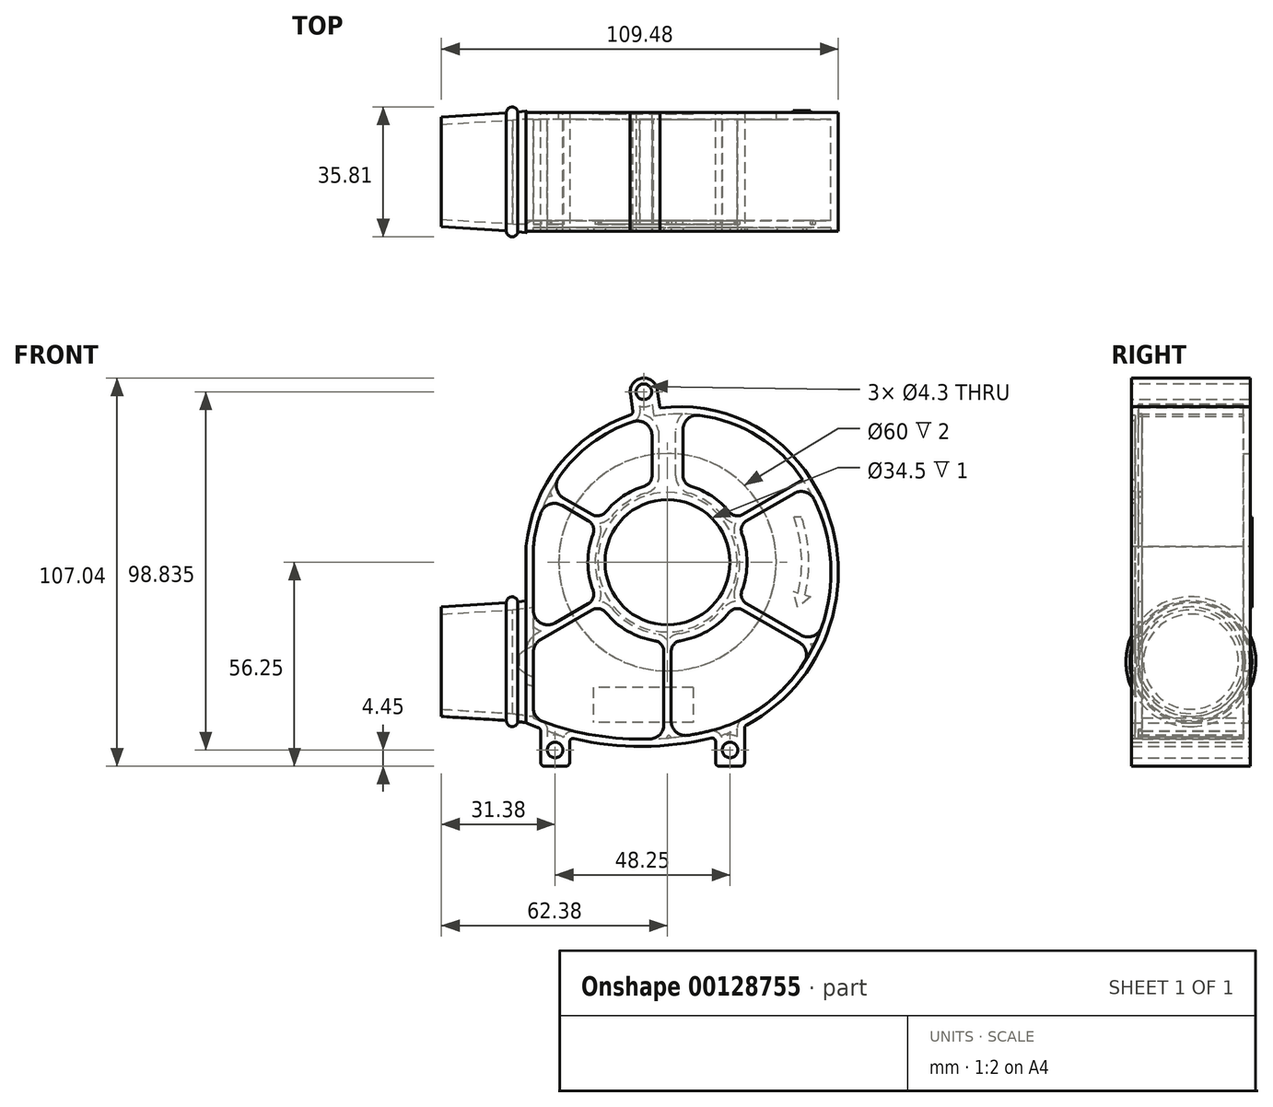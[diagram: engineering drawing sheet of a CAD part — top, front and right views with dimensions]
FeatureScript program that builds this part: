
annotation { "Feature Type Name" : "Feature", "Feature Type Description" : "" }
export const myFeature = defineFeature(function(context is Context, id is Id, definition is map)
    precondition{}
    {
        {
            var Q0;
            Q0=qCreatedBy(makeId("Front.planeOp"),FACE);
            var sketch = newSketch(context, id + "F0", { "sketchPlane" : qUnion([Q0])});
            skLineSegment(sketch, "E0", {"start": v(0, 0) * mm, "end": v(0, 15) * mm, "construction": true});
            skLineSegment(sketch, "E1", {"start": v(0, 15) * mm, "end": v(7.5, 13) * mm, "construction": true});
            skLineSegment(sketch, "E2", {"start": v(7.5, 13) * mm, "end": v(0, 0) * mm, "construction": true});
            skCircle(sketch, "E3.cCircle", {"center": v(0, 0) * mm, "radius": 220.7 * mm, "construction": true});
            skLineSegment(sketch, "E3.0", {"start": v(0, 254.83) * mm, "end": v(220.7, 127.42) * mm, "construction": true});
            skLineSegment(sketch, "E3.1", {"start": v(220.7, 127.42) * mm, "end": v(220.7, -127.42) * mm, "construction": true});
            skLineSegment(sketch, "E3.2", {"start": v(220.7, -127.42) * mm, "end": v(0, -254.83) * mm, "construction": true});
            skLineSegment(sketch, "E3.3", {"start": v(0, -254.83) * mm, "end": v(-220.7, -127.42) * mm, "construction": true});
            skLineSegment(sketch, "E3.4", {"start": v(-220.7, -127.42) * mm, "end": v(-220.7, 127.42) * mm, "construction": true});
            skLineSegment(sketch, "E3.5", {"start": v(-220.7, 127.42) * mm, "end": v(0, 254.83) * mm, "construction": true});
            skPoint(sketch, "E3.0.midPoint", {"position": v(110.35, 191.13) * mm});
            skLineSegment(sketch, "E4", {"start": v(110.35, 191.13) * mm, "end": v(7.5, 13) * mm, "construction": true});
            skCircle(sketch, "E5", {"center": v(0, 0) * mm, "radius": 17 * mm, "construction": true});
            skCircle(sketch, "E6", {"center": v(0, 0) * mm, "radius": 22 * mm, "construction": true});
            skLineSegment(sketch, "E7", {"start": v(0, 254.83) * mm, "end": v(0, -254.83) * mm, "construction": true});
            skLineSegment(sketch, "E8", {"start": v(220.7, -127.42) * mm, "end": v(-220.7, 127.42) * mm, "construction": true});
            skLineSegment(sketch, "E9", {"start": v(0, 0) * mm, "end": v(220.7, 127.42) * mm, "construction": true});
            skLineSegment(sketch, "E10", {"start": v(0, 0) * mm, "end": v(-220.7, -127.42) * mm, "construction": true});
            skArc(sketch, "E11", {"start": v(0, 39.25) * mm, "mid": v(-26.14, 29.28) * mm, "end": v(-39, 4.42) * mm, "construction": true});
            skArc(sketch, "E12", {"start": v(-33.38, -37.9) * mm, "mid": v(-17.84, -47.24) * mm, "end": v(0, -50.5) * mm, "construction": true});
            skArc(sketch, "E13.trimOffspring", {"start": v(37.02, 21.37) * mm, "mid": v(21.37, 37.02) * mm, "end": v(0, 42.75) * mm, "construction": true});
            skArc(sketch, "E14.trimOffspring", {"start": v(39.62, -22.87) * mm, "mid": v(45.75, 0) * mm, "end": v(39.62, 22.88) * mm, "construction": true});
            skArc(sketch, "E15.trimOffspring", {"start": v(0, -48.5) * mm, "mid": v(24.25, -42) * mm, "end": v(42, -24.25) * mm, "construction": true});
            skLineSegment(sketch, "E16", {"start": v(-39, 4.42) * mm, "end": v(-39, -44.27) * mm});
            skLineSegment(sketch, "E17", {"start": v(-39, -44.27) * mm, "end": v(0, 0) * mm, "construction": true});
            skArc(sketch, "E18", {"start": v(39.62, 22.88) * mm, "mid": v(-6.29, 41.76) * mm, "end": v(-39, 4.42) * mm});
            skArc(sketch, "E19", {"start": v(21.25, -45.2) * mm, "mid": v(45.46, -15.22) * mm, "end": v(39.62, 22.88) * mm});
            skArc(sketch, "E20", {"start": v(-39, -44.27) * mm, "mid": v(-37.01, -45.1) * mm, "end": v(-35, -45.86) * mm});
            skPoint(sketch, "E20.third.point", {"position": v(17.1, -47.1) * mm});
            skLineSegment(sketch, "E21", {"start": v(-56.08, -56.25) * mm, "end": v(101.71, -56.25) * mm, "construction": true});
            skLineSegment(sketch, "E22.bottom", {"start": v(-35, -56.25) * mm, "end": v(-27, -56.25) * mm});
            skLineSegment(sketch, "E22.top", {"start": v(-35, -39.71) * mm, "end": v(-34.98, -39.71) * mm});
            skLineSegment(sketch, "E22.left", {"start": v(-35, -56.25) * mm, "end": v(-35, -45.86) * mm});
            skLineSegment(sketch, "E22.right", {"start": v(-27, -56.25) * mm, "end": v(-27, -48.34) * mm});
            skLineSegment(sketch, "E23.bottom", {"start": v(13.25, -56.25) * mm, "end": v(21.25, -56.25) * mm});
            skLineSegment(sketch, "E23.left", {"start": v(13.25, -56.25) * mm, "end": v(13.25, -48.2) * mm});
            skLineSegment(sketch, "E23.right", {"start": v(21.25, -56.25) * mm, "end": v(21.25, -45.2) * mm});
            skLineSegment(sketch, "E24.trimOffspring", {"start": v(-35, -39.73) * mm, "end": v(-35, -39.71) * mm});
            skArc(sketch, "E25.trimOffspring", {"start": v(-27, -48.34) * mm, "mid": v(-6.87, -50.82) * mm, "end": v(13.25, -48.2) * mm});
            skLineSegment(sketch, "E26", {"start": v(17.25, -56.25) * mm, "end": v(17.25, -51.8) * mm, "construction": true});
            skLineSegment(sketch, "E27", {"start": v(17.25, -51.8) * mm, "end": v(-31, -51.8) * mm, "construction": true});
            skLineSegment(sketch, "E28", {"start": v(-31, -51.8) * mm, "end": v(-31, -56.25) * mm, "construction": true});
            skCircle(sketch, "E29", {"center": v(-31, -51.8) * mm, "radius": 2.15 * mm});
            skCircle(sketch, "E30", {"center": v(17.25, -51.8) * mm, "radius": 2.15 * mm});
            skSolve(sketch);
        }
        {
            var Q0;
            Q0=makeQuery(id+"F0.imprint","IMPRINT",FACE,{"disambiguationData":[TD([[makeQuery(id+"F0.imprint","IMPRINT",EDGE,{"derivedFrom":sQuery(id+"F0.wireOp",EDGE,"E16")}),1.0]])]});
            extrude(context, id + "F1", {"entities" : qUnion([Q0]), "depth" : 32.85 * mm});
        }
        {
            var Q0;
            Q0=makeQuery(id+"F1.opExtrude","CAP_FACE",FACE,{"disambiguationData":[OSD([sQuery(id+"F0.wireOp",EDGE,"E16"),sQuery(id+"F0.wireOp",EDGE,"E18"),sQuery(id+"F0.wireOp",EDGE,"E19"),sQuery(id+"F0.wireOp",EDGE,"E20"),sQuery(id+"F0.wireOp",EDGE,"E22.bottom"),sQuery(id+"F0.wireOp",EDGE,"E22.left"),sQuery(id+"F0.wireOp",EDGE,"E22.right"),sQuery(id+"F0.wireOp",EDGE,"E23.bottom"),sQuery(id+"F0.wireOp",EDGE,"E23.left"),sQuery(id+"F0.wireOp",EDGE,"E23.right"),sQuery(id+"F0.wireOp",EDGE,"E25.trimOffspring"),sQuery(id+"F0.wireOp",EDGE,"E29"),sQuery(id+"F0.wireOp",EDGE,"E30")])],"isStart":false});
            var sketch = newSketch(context, id + "F2", { "sketchPlane" : qUnion([Q0])});
            skArc(sketch, "E31.0", {"start": v(-37, -42.94) * mm, "mid": v(-35.66, -43.48) * mm, "end": v(-34.31, -43.99) * mm});
            skLineSegment(sketch, "E31.1", {"start": v(-37, 4.32) * mm, "end": v(-37, -20.2) * mm});
            skArc(sketch, "E31.2", {"start": v(37.93, 21.8) * mm, "mid": v(37.9, 21.84) * mm, "end": v(37.89, 21.87) * mm});
            skArc(sketch, "E31.3", {"start": v(30.22, -36.54) * mm, "mid": v(35.55, -30.75) * mm, "end": v(39.8, -24.14) * mm});
            skArc(sketch, "E32", {"start": v(-34.31, -43.99) * mm, "mid": v(-17.9, -48.08) * mm, "end": v(-1, -48.58) * mm});
            skPoint(sketch, "E33.third.point", {"position": v(30.22, -36.54) * mm});
            skArc(sketch, "E34.trimOffspring", {"start": v(12.23, -46.4) * mm, "mid": v(21.86, -42.63) * mm, "end": v(30.22, -36.54) * mm});
            skArc(sketch, "E35", {"start": v(-20.53, 7.79) * mm, "mid": v(-21.95, 0) * mm, "end": v(-20.53, -7.79) * mm});
            skCircle(sketch, "E36", {"center": v(0, 0) * mm, "radius": 17.25 * mm});
            skLineSegment(sketch, "E37", {"start": v(0, 21.95) * mm, "end": v(0, 40.74) * mm, "construction": true});
            skLineSegment(sketch, "E38", {"start": v(19.01, 10.98) * mm, "end": v(37.89, 21.87) * mm, "construction": true});
            skLineSegment(sketch, "E39", {"start": v(19.01, -10.98) * mm, "end": v(40.27, -23.25) * mm, "construction": true});
            skLineSegment(sketch, "E40", {"start": v(-19.01, 10.98) * mm, "end": v(-32.68, 18.87) * mm, "construction": true});
            skLineSegment(sketch, "E41", {"start": v(-19.01, -10.98) * mm, "end": v(-37, -21.36) * mm, "construction": true});
            skLineSegment(sketch, "E42", {"start": v(0, -21.95) * mm, "end": v(0, -48.5) * mm, "construction": true});
            skLineSegment(sketch, "E43.0", {"start": v(4.28, 23.87) * mm, "end": v(4.28, 40.88) * mm});
            skLineSegment(sketch, "E44.0", {"start": v(-4.28, 23.87) * mm, "end": v(-4.28, 40.15) * mm});
            skLineSegment(sketch, "E45.0", {"start": v(21.83, 11.45) * mm, "end": v(38.42, 21.03) * mm});
            skLineSegment(sketch, "E46.0", {"start": v(20.83, -13.18) * mm, "end": v(39.8, -24.14) * mm});
            skLineSegment(sketch, "E47.0", {"start": v(-1, -24.63) * mm, "end": v(-1, -48.58) * mm});
            skLineSegment(sketch, "E48.0", {"start": v(-21.83, -11.45) * mm, "end": v(-37, -20.2) * mm});
            skLineSegment(sketch, "E49.0", {"start": v(-21.83, 11.45) * mm, "end": v(-33.13, 17.97) * mm});
            skLineSegment(sketch, "E50.0", {"start": v(-20.83, 13.18) * mm, "end": v(-32.21, 19.75) * mm});
            skLineSegment(sketch, "E51.0", {"start": v(1, -24.63) * mm, "end": v(1, -48.4) * mm});
            skLineSegment(sketch, "E52.0", {"start": v(21.83, -11.45) * mm, "end": v(40.7, -22.35) * mm});
            skLineSegment(sketch, "E53.0", {"start": v(20.83, 13.18) * mm, "end": v(37.34, 22.72) * mm});
            skLineSegment(sketch, "E54.0", {"start": v(-20.83, -13.18) * mm, "end": v(-37, -22.52) * mm});
            skArc(sketch, "E55.trimOffspring", {"start": v(-33.13, 17.97) * mm, "mid": v(-35.66, 11.32) * mm, "end": v(-37, 4.32) * mm});
            skArc(sketch, "E56.trimOffspring", {"start": v(-6.4, 21) * mm, "mid": v(-12.24, 18.23) * mm, "end": v(-17, 13.88) * mm});
            skArc(sketch, "E57.trimOffspring", {"start": v(-4.28, 40.15) * mm, "mid": v(-20.52, 33.07) * mm, "end": v(-32.21, 19.75) * mm});
            skArc(sketch, "E58.trimOffspring", {"start": v(37.34, 22.72) * mm, "mid": v(23.05, 35.86) * mm, "end": v(4.28, 40.88) * mm});
            skArc(sketch, "E59.trimOffspring", {"start": v(17, 13.88) * mm, "mid": v(12.24, 18.23) * mm, "end": v(6.4, 21) * mm});
            skArc(sketch, "E60.trimOffspring", {"start": v(40.7, -22.35) * mm, "mid": v(45.04, -0.37) * mm, "end": v(38.42, 21.03) * mm});
            skArc(sketch, "E61.trimOffspring", {"start": v(20.53, -7.79) * mm, "mid": v(21.96, 0) * mm, "end": v(20.53, 7.79) * mm});
            skArc(sketch, "E62.trimOffspring", {"start": v(1, -48.4) * mm, "mid": v(6.91, -47.55) * mm, "end": v(12.75, -46.27) * mm});
            skArc(sketch, "E63.trimOffspring", {"start": v(3.52, -21.67) * mm, "mid": v(10.98, -19.01) * mm, "end": v(17, -13.88) * mm});
            skLineSegment(sketch, "E64.trimOffspring", {"start": v(-37, -22.52) * mm, "end": v(-37, -42.94) * mm});
            skArc(sketch, "E65.trimOffspring", {"start": v(-17, -13.88) * mm, "mid": v(-10.98, -19.01) * mm, "end": v(-3.52, -21.67) * mm});
            skPoint(sketch, "E66.visualSharp", {"position": v(1, -21.93) * mm});
            skArc(sketch, "E66.filletArc", {"start": v(3.52, -21.67) * mm, "mid": v(1.71, -22.69) * mm, "end": v(1, -24.63) * mm});
            skPoint(sketch, "E67.visualSharp", {"position": v(18.5, -11.83) * mm});
            skArc(sketch, "E67.filletArc", {"start": v(20.83, -13.18) * mm, "mid": v(18.8, -12.83) * mm, "end": v(17, -13.88) * mm});
            skPoint(sketch, "E68.visualSharp", {"position": v(19.5, -10.1) * mm});
            skArc(sketch, "E68.filletArc", {"start": v(20.53, -7.79) * mm, "mid": v(20.5, -9.86) * mm, "end": v(21.83, -11.45) * mm});
            skPoint(sketch, "E69.visualSharp", {"position": v(19.5, 10.1) * mm});
            skArc(sketch, "E69.filletArc", {"start": v(21.83, 11.45) * mm, "mid": v(20.5, 9.86) * mm, "end": v(20.53, 7.79) * mm});
            skPoint(sketch, "E70.visualSharp", {"position": v(18.5, 11.83) * mm});
            skArc(sketch, "E70.filletArc", {"start": v(17, 13.88) * mm, "mid": v(18.8, 12.83) * mm, "end": v(20.83, 13.18) * mm});
            skPoint(sketch, "E71.visualSharp", {"position": v(4.28, 21.53) * mm});
            skArc(sketch, "E71.filletArc", {"start": v(4.28, 23.87) * mm, "mid": v(4.87, 22.08) * mm, "end": v(6.4, 21) * mm});
            skPoint(sketch, "E72.visualSharp", {"position": v(-4.28, 21.53) * mm});
            skArc(sketch, "E72.filletArc", {"start": v(-6.4, 21) * mm, "mid": v(-4.87, 22.08) * mm, "end": v(-4.28, 23.87) * mm});
            skPoint(sketch, "E73.visualSharp", {"position": v(-19.5, 10.1) * mm});
            skArc(sketch, "E73.filletArc", {"start": v(-20.53, 7.79) * mm, "mid": v(-20.5, 9.86) * mm, "end": v(-21.83, 11.45) * mm});
            skPoint(sketch, "E74.visualSharp", {"position": v(-18.5, 11.83) * mm});
            skArc(sketch, "E74.filletArc", {"start": v(-20.83, 13.18) * mm, "mid": v(-18.8, 12.83) * mm, "end": v(-17, 13.88) * mm});
            skPoint(sketch, "E75.visualSharp", {"position": v(-19.5, -10.1) * mm});
            skArc(sketch, "E75.filletArc", {"start": v(-21.83, -11.45) * mm, "mid": v(-20.5, -9.86) * mm, "end": v(-20.53, -7.79) * mm});
            skPoint(sketch, "E76.visualSharp", {"position": v(-18.5, -11.83) * mm});
            skArc(sketch, "E76.filletArc", {"start": v(-17, -13.88) * mm, "mid": v(-18.8, -12.83) * mm, "end": v(-20.83, -13.18) * mm});
            skPoint(sketch, "E77.visualSharp", {"position": v(-1, -21.93) * mm});
            skArc(sketch, "E77.filletArc", {"start": v(-1, -24.63) * mm, "mid": v(-1.71, -22.69) * mm, "end": v(-3.52, -21.67) * mm});
            skSolve(sketch);
        }
        {
            var Q0;
            Q0 = qSketchRegion(id + "F2", true);
            extrude(context, id + "F3", {"entities" : qUnion([Q0]), "operationType" : NewBodyOperationType.REMOVE, "oppositeDirection" : true, "depth" : 1 * mm});
        }
        {
            var Q0;
            Q0=makeQuery(id+"F3.boolean.opBoolean","COPY",EDGE,{"derivedFrom":makeQuery(id+"F3.opExtrude","SWEPT_EDGE",EDGE,{"disambiguationData":[OSD([sQuery(id+"F2.wireOp",EDGE,"E54.0"),sQuery(id+"F2.wireOp",EDGE,"E64.trimOffspring")])]})});
            var Q1;
            Q1=makeQuery(id+"F3.boolean.opBoolean","COPY",EDGE,{"derivedFrom":makeQuery(id+"F3.opExtrude","SWEPT_EDGE",EDGE,{"disambiguationData":[OSD([sQuery(id+"F2.wireOp",EDGE,"E49.0"),sQuery(id+"F2.wireOp",EDGE,"E55.trimOffspring")])]})});
            var Q2;
            Q2=makeQuery(id+"F3.boolean.opBoolean","COPY",EDGE,{"derivedFrom":makeQuery(id+"F3.opExtrude","SWEPT_EDGE",EDGE,{"disambiguationData":[OSD([sQuery(id+"F2.wireOp",EDGE,"E44.0"),sQuery(id+"F2.wireOp",EDGE,"E57.trimOffspring")])]})});
            var Q3;
            Q3=makeQuery(id+"F3.boolean.opBoolean","COPY",EDGE,{"derivedFrom":makeQuery(id+"F3.opExtrude","SWEPT_EDGE",EDGE,{"disambiguationData":[OSD([sQuery(id+"F2.wireOp",EDGE,"E45.0"),sQuery(id+"F2.wireOp",EDGE,"E60.trimOffspring")])]})});
            var Q4;
            Q4=makeQuery(id+"F3.boolean.opBoolean","COPY",EDGE,{"derivedFrom":makeQuery(id+"F3.opExtrude","SWEPT_EDGE",EDGE,{"disambiguationData":[OSD([sQuery(id+"F2.wireOp",EDGE,"E31.3"),sQuery(id+"F2.wireOp",EDGE,"E46.0")])]})});
            var Q5;
            Q5=makeQuery(id+"F3.boolean.opBoolean","COPY",EDGE,{"derivedFrom":makeQuery(id+"F3.opExtrude","SWEPT_EDGE",EDGE,{"disambiguationData":[OSD([sQuery(id+"F2.wireOp",EDGE,"E52.0"),sQuery(id+"F2.wireOp",EDGE,"E60.trimOffspring")])]})});
            var Q6;
            Q6=makeQuery(id+"F3.boolean.opBoolean","COPY",EDGE,{"derivedFrom":makeQuery(id+"F3.opExtrude","SWEPT_EDGE",EDGE,{"disambiguationData":[OSD([sQuery(id+"F2.wireOp",EDGE,"E51.0"),sQuery(id+"F2.wireOp",EDGE,"E62.trimOffspring")])]})});
            var Q7;
            Q7=makeQuery(id+"F3.boolean.opBoolean","COPY",EDGE,{"derivedFrom":makeQuery(id+"F3.opExtrude","SWEPT_EDGE",EDGE,{"disambiguationData":[OSD([sQuery(id+"F2.wireOp",EDGE,"E31.0"),sQuery(id+"F2.wireOp",EDGE,"E64.trimOffspring")])]})});
            var Q8;
            Q8=makeQuery(id+"F3.boolean.opBoolean","COPY",EDGE,{"derivedFrom":makeQuery(id+"F3.opExtrude","SWEPT_EDGE",EDGE,{"disambiguationData":[OSD([sQuery(id+"F2.wireOp",EDGE,"E50.0"),sQuery(id+"F2.wireOp",EDGE,"E57.trimOffspring")])]})});
            var Q9;
            Q9=makeQuery(id+"F3.boolean.opBoolean","COPY",EDGE,{"derivedFrom":makeQuery(id+"F3.opExtrude","SWEPT_EDGE",EDGE,{"disambiguationData":[OSD([sQuery(id+"F2.wireOp",EDGE,"E31.1"),sQuery(id+"F2.wireOp",EDGE,"E48.0")])]})});
            var Q10;
            Q10=makeQuery(id+"F3.boolean.opBoolean","COPY",EDGE,{"derivedFrom":makeQuery(id+"F3.opExtrude","SWEPT_EDGE",EDGE,{"disambiguationData":[OSD([sQuery(id+"F2.wireOp",EDGE,"E43.0"),sQuery(id+"F2.wireOp",EDGE,"E58.trimOffspring")])]})});
            var Q11;
            Q11=makeQuery(id+"F3.boolean.opBoolean","COPY",EDGE,{"derivedFrom":makeQuery(id+"F3.opExtrude","SWEPT_EDGE",EDGE,{"disambiguationData":[OSD([sQuery(id+"F2.wireOp",EDGE,"E32"),sQuery(id+"F2.wireOp",EDGE,"E47.0")])]})});
            fillet(context, id + "F4", {"entities" : qUnion([Q0, Q1, Q2, Q3, Q4, Q5, Q6, Q7, Q8, Q9, Q10, Q11]), "radius" : 4 * mm, "tangentPropagation" : true, "allowEdgeOverflow" : false});
        }
        {
            var Q0;
            Q0=makeQuery(id+"F1.opExtrude","SWEPT_EDGE",EDGE,{"disambiguationData":[OSD([sQuery(id+"F0.wireOp",EDGE,"E22.bottom"),sQuery(id+"F0.wireOp",EDGE,"E22.left")])]});
            var Q1;
            Q1=makeQuery(id+"F1.opExtrude","SWEPT_EDGE",EDGE,{"disambiguationData":[OSD([sQuery(id+"F0.wireOp",EDGE,"E22.bottom"),sQuery(id+"F0.wireOp",EDGE,"E22.right")])]});
            var Q2;
            Q2=makeQuery(id+"F1.opExtrude","SWEPT_EDGE",EDGE,{"disambiguationData":[OSD([sQuery(id+"F0.wireOp",EDGE,"E23.bottom"),sQuery(id+"F0.wireOp",EDGE,"E23.left")])]});
            var Q3;
            Q3=makeQuery(id+"F1.opExtrude","SWEPT_EDGE",EDGE,{"disambiguationData":[OSD([sQuery(id+"F0.wireOp",EDGE,"E23.bottom"),sQuery(id+"F0.wireOp",EDGE,"E23.right")])]});
            var Q4;
            Q4=makeQuery(id+"F1.opExtrude","SWEPT_EDGE",EDGE,{"disambiguationData":[OSD([sQuery(id+"F0.wireOp",EDGE,"E23.left"),sQuery(id+"F0.wireOp",EDGE,"E25.trimOffspring")])]});
            var Q5;
            Q5=makeQuery(id+"F1.opExtrude","SWEPT_EDGE",EDGE,{"disambiguationData":[OSD([sQuery(id+"F0.wireOp",EDGE,"E20"),sQuery(id+"F0.wireOp",EDGE,"E22.left")])]});
            var Q6;
            Q6=makeQuery(id+"F1.opExtrude","SWEPT_EDGE",EDGE,{"disambiguationData":[OSD([sQuery(id+"F0.wireOp",EDGE,"E19"),sQuery(id+"F0.wireOp",EDGE,"E23.right")])]});
            var Q7;
            Q7=makeQuery(id+"F1.opExtrude","SWEPT_EDGE",EDGE,{"disambiguationData":[OSD([sQuery(id+"F0.wireOp",EDGE,"E22.right"),sQuery(id+"F0.wireOp",EDGE,"E25.trimOffspring")])]});
            fillet(context, id + "F5", {"entities" : qUnion([Q0, Q1, Q2, Q3, Q4, Q5, Q6, Q7]), "radius" : 1 * mm, "tangentPropagation" : true, "allowEdgeOverflow" : false});
        }
        {
            var Q0;
            Q0=makeQuery(id+"F1.opExtrude","CAP_FACE",FACE,{"disambiguationData":[OSD([sQuery(id+"F0.wireOp",EDGE,"E16"),sQuery(id+"F0.wireOp",EDGE,"E18"),sQuery(id+"F0.wireOp",EDGE,"E19"),sQuery(id+"F0.wireOp",EDGE,"E20"),sQuery(id+"F0.wireOp",EDGE,"E22.bottom"),sQuery(id+"F0.wireOp",EDGE,"E22.left"),sQuery(id+"F0.wireOp",EDGE,"E22.right"),sQuery(id+"F0.wireOp",EDGE,"E23.bottom"),sQuery(id+"F0.wireOp",EDGE,"E23.left"),sQuery(id+"F0.wireOp",EDGE,"E23.right"),sQuery(id+"F0.wireOp",EDGE,"E25.trimOffspring"),sQuery(id+"F0.wireOp",EDGE,"E29"),sQuery(id+"F0.wireOp",EDGE,"E30")])],"isStart":false});
            var Q1;
            Q1=makeQuery(id+"F1.opExtrude","CAP_FACE",FACE,{"disambiguationData":[OSD([sQuery(id+"F0.wireOp",EDGE,"E16"),sQuery(id+"F0.wireOp",EDGE,"E18"),sQuery(id+"F0.wireOp",EDGE,"E19"),sQuery(id+"F0.wireOp",EDGE,"E20"),sQuery(id+"F0.wireOp",EDGE,"E22.bottom"),sQuery(id+"F0.wireOp",EDGE,"E22.left"),sQuery(id+"F0.wireOp",EDGE,"E22.right"),sQuery(id+"F0.wireOp",EDGE,"E23.bottom"),sQuery(id+"F0.wireOp",EDGE,"E23.left"),sQuery(id+"F0.wireOp",EDGE,"E23.right"),sQuery(id+"F0.wireOp",EDGE,"E25.trimOffspring"),sQuery(id+"F0.wireOp",EDGE,"E29"),sQuery(id+"F0.wireOp",EDGE,"E30")])],"isStart":true});
            cPlane(context, id + "F6", {"entities" : qUnion([Q0, Q1]), "cplaneType" : CPlaneType.MID_PLANE, "offset" : 25 * mm, "width" : 150 * mm, "height" : 150 * mm});
        }
        {
            var Q0;
            Q0=qCreatedBy(id+"F6.planeOp",FACE);
            var sketch = newSketch(context, id + "F7", { "sketchPlane" : qUnion([Q0])});
            skLineSegment(sketch, "E78", {"start": v(-39, -10.62) * mm, "end": v(-39, -44.27) * mm, "construction": true});
            skLineSegment(sketch, "E79", {"start": v(-39, -27.45) * mm, "end": v(-62.38, -27.45) * mm});
            skLineSegment(sketch, "E80", {"start": v(-62.38, -27.45) * mm, "end": v(-62.38, -42.55) * mm});
            skLineSegment(sketch, "E81", {"start": v(-62.38, -42.55) * mm, "end": v(-44.45, -43.66) * mm});
            skLineSegment(sketch, "E82", {"start": v(-41.26, -43.97) * mm, "end": v(-39, -44.27) * mm});
            skArc(sketch, "E83", {"start": v(-44.45, -43.66) * mm, "mid": v(-43, -45.35) * mm, "end": v(-41.26, -43.97) * mm});
            skLineSegment(sketch, "E84", {"start": v(-39, -27.45) * mm, "end": v(-39, -44.27) * mm});
            skSolve(sketch);
        }
        {
            var Q0;
            Q0 = qSketchRegion(id + "F7", true);
            var Q1;
            Q1=sQuery(id+"F7.wireOp",EDGE,"E79");
            revolve(context, id + "F8", {"operationType" : NewBodyOperationType.ADD, "entities" : qUnion([Q0]), "axis" : qUnion([Q1]), "revolveType" : RevolveType.FULL});
        }
        {
            var Q0;
            Q0=makeQuery(id+"F1.opExtrude","CAP_FACE",FACE,{"disambiguationData":[OSD([sQuery(id+"F0.wireOp",EDGE,"E16"),sQuery(id+"F0.wireOp",EDGE,"E18"),sQuery(id+"F0.wireOp",EDGE,"E19"),sQuery(id+"F0.wireOp",EDGE,"E20"),sQuery(id+"F0.wireOp",EDGE,"E22.bottom"),sQuery(id+"F0.wireOp",EDGE,"E22.left"),sQuery(id+"F0.wireOp",EDGE,"E22.right"),sQuery(id+"F0.wireOp",EDGE,"E23.bottom"),sQuery(id+"F0.wireOp",EDGE,"E23.left"),sQuery(id+"F0.wireOp",EDGE,"E23.right"),sQuery(id+"F0.wireOp",EDGE,"E25.trimOffspring"),sQuery(id+"F0.wireOp",EDGE,"E29"),sQuery(id+"F0.wireOp",EDGE,"E30")])],"isStart":false});
            var sketch = newSketch(context, id + "F9", { "sketchPlane" : qUnion([Q0])});
            skCircle(sketch, "E85", {"center": v(0, 0) * mm, "radius": 51.24 * mm, "construction": true});
            skLineSegment(sketch, "E86", {"start": v(0, 0) * mm, "end": v(-7.04, 50.75) * mm, "construction": true});
            skLineSegment(sketch, "E87", {"start": v(-3.3, 51.13) * mm, "end": v(3.71, 0.52) * mm, "construction": true});
            skLineSegment(sketch, "E88", {"start": v(-10.73, 50.1) * mm, "end": v(-3.71, -0.52) * mm, "construction": true});
            skLineSegment(sketch, "E89", {"start": v(-3.71, -0.52) * mm, "end": v(3.71, 0.52) * mm, "construction": true});
            skArc(sketch, "E90", {"start": v(-2.8, 47.55) * mm, "mid": v(-7.04, 50.75) * mm, "end": v(-10.24, 46.52) * mm});
            skPoint(sketch, "E90.first.point", {"position": v(-2.8, 47.55) * mm});
            skPoint(sketch, "E90.second.point", {"position": v(-10.24, 46.52) * mm});
            skCircle(sketch, "E91", {"center": v(-6.52, 47.04) * mm, "radius": 2.15 * mm});
            skArc(sketch, "E92.0", {"start": v(-2.11, 42.53) * mm, "mid": v(-5.82, 41.87) * mm, "end": v(-9.46, 40.89) * mm});
            skPoint(sketch, "E93.orphan", {"position": v(-39, 4.42) * mm});
            skPoint(sketch, "E94.orphan", {"position": v(39.62, 22.88) * mm});
            skLineSegment(sketch, "E95", {"start": v(-2.8, 47.55) * mm, "end": v(-2.11, 42.53) * mm});
            skLineSegment(sketch, "E96", {"start": v(-10.24, 46.52) * mm, "end": v(-9.46, 40.89) * mm});
            skSolve(sketch);
        }
        {
            var Q0;
            Q0=makeQuery(id+"F9.imprint","IMPRINT",FACE,{"disambiguationData":[TD([[makeQuery(id+"F9.imprint","IMPRINT",EDGE,{"derivedFrom":sQuery(id+"F9.wireOp",EDGE,"E90")}),1.0]])]});
            var Q1;
            Q1=makeQuery(id+"F1.opExtrude","CAP_FACE",FACE,{"disambiguationData":[OSD([sQuery(id+"F0.wireOp",EDGE,"E16"),sQuery(id+"F0.wireOp",EDGE,"E18"),sQuery(id+"F0.wireOp",EDGE,"E19"),sQuery(id+"F0.wireOp",EDGE,"E20"),sQuery(id+"F0.wireOp",EDGE,"E22.bottom"),sQuery(id+"F0.wireOp",EDGE,"E22.left"),sQuery(id+"F0.wireOp",EDGE,"E22.right"),sQuery(id+"F0.wireOp",EDGE,"E23.bottom"),sQuery(id+"F0.wireOp",EDGE,"E23.left"),sQuery(id+"F0.wireOp",EDGE,"E23.right"),sQuery(id+"F0.wireOp",EDGE,"E25.trimOffspring"),sQuery(id+"F0.wireOp",EDGE,"E29"),sQuery(id+"F0.wireOp",EDGE,"E30")])],"isStart":true});
            extrude(context, id + "F10", {"entities" : qUnion([Q0]), "operationType" : NewBodyOperationType.ADD, "endBound" : BoundingType.UP_TO_SURFACE, "oppositeDirection" : true, "endBoundEntityFace" : qUnion([Q1]), "depth" : 25 * mm});
        }
        {
            var Q0;
            Q0=makeQuery(id+"F10.opExtrude","SWEPT_EDGE",EDGE,{"disambiguationData":[OSD([sQuery(id+"F0.wireOp",EDGE,"E18"),sQuery(id+"F9.wireOp",EDGE,"E92.0"),sQuery(id+"F9.wireOp",EDGE,"E96")])]});
            var Q1;
            Q1=makeQuery(id+"F10.opExtrude","SWEPT_EDGE",EDGE,{"disambiguationData":[OSD([sQuery(id+"F0.wireOp",EDGE,"E18"),sQuery(id+"F9.wireOp",EDGE,"E92.0"),sQuery(id+"F9.wireOp",EDGE,"E95")])]});
            fillet(context, id + "F11", {"entities" : qUnion([Q0, Q1]), "radius" : 1 * mm, "tangentPropagation" : true, "allowEdgeOverflow" : false});
        }
        {
            var Q0;
            {var subQ0=sQuery(id+"F0.wireOp",EDGE,"E30");var subQ1=sQuery(id+"F0.wireOp",EDGE,"E29");var subQ2=sQuery(id+"F0.wireOp",EDGE,"E25.trimOffspring");var subQ3=sQuery(id+"F0.wireOp",EDGE,"E23.right");var subQ4=sQuery(id+"F0.wireOp",EDGE,"E23.left");var subQ5=sQuery(id+"F0.wireOp",EDGE,"E23.bottom");var subQ6=sQuery(id+"F0.wireOp",EDGE,"E22.right");var subQ7=sQuery(id+"F0.wireOp",EDGE,"E22.left");var subQ8=sQuery(id+"F0.wireOp",EDGE,"E22.bottom");var subQ9=sQuery(id+"F0.wireOp",EDGE,"E20");var subQ10=sQuery(id+"F0.wireOp",EDGE,"E19");var subQ11=sQuery(id+"F0.wireOp",EDGE,"E18");var subQ12=sQuery(id+"F0.wireOp",EDGE,"E16");Q0=makeQuery(id+"F10.boolean.opBoolean","MERGE",FACE,{"derivedFrom":[makeQuery(id+"F1.opExtrude","CAP_FACE",FACE,{"disambiguationData":[OSD([subQ12,subQ11,subQ10,subQ9,subQ8,subQ7,subQ6,subQ5,subQ4,subQ3,subQ2,subQ1,subQ0])],"isStart":true}),makeQuery(id+"F10.opExtrude","CAP_FACE",FACE,{"disambiguationData":[OSD([subQ12,subQ11,subQ10,subQ9,subQ8,subQ7,subQ6,subQ5,subQ4,subQ3,subQ2,subQ1,subQ0])],"isStart":false})]});}
            var sketch = newSketch(context, id + "F12", { "sketchPlane" : qUnion([Q0])});
            skCircle(sketch, "E97", {"center": v(0, 0) * mm, "radius": 30 * mm});
            skSolve(sketch);
        }
        {
            var Q0;
            Q0 = qSketchRegion(id + "F12", true);
            extrude(context, id + "F13", {"entities" : qUnion([Q0]), "operationType" : NewBodyOperationType.REMOVE, "oppositeDirection" : true, "depth" : 5 * mm});
        }
        {
            var Q0;
            Q0=makeQuery(id+"F8.opRevolve","SWEPT_FACE",FACE,{"disambiguationData":[OSD([sQuery(id+"F7.wireOp",EDGE,"E80")])]});
            var Q1;
            Q1=makeQuery(id+"F13.boolean.opBoolean","COPY",FACE,{"derivedFrom":makeQuery(id+"F13.opExtrude","CAP_FACE",FACE,{"disambiguationData":[OSD([sQuery(id+"F12.wireOp",EDGE,"E97")])],"isStart":false})});
            var Q2;
            Q2=makeQuery(id+"F13.boolean.opBoolean","COPY",FACE,{"derivedFrom":makeQuery(id+"F13.opExtrude","SWEPT_FACE",FACE,{"disambiguationData":[OSD([sQuery(id+"F12.wireOp",EDGE,"E97")])]})});
            shell(context, id + "F14", {"entities" : qUnion([Q0, Q1, Q2]), "thickness" : 2 * mm});
        }
        {
            var Q0;
            {var subQ0=sQuery(id+"F0.wireOp",EDGE,"E30");var subQ1=sQuery(id+"F0.wireOp",EDGE,"E29");var subQ2=sQuery(id+"F0.wireOp",EDGE,"E25.trimOffspring");var subQ3=sQuery(id+"F0.wireOp",EDGE,"E23.right");var subQ4=sQuery(id+"F0.wireOp",EDGE,"E23.left");var subQ5=sQuery(id+"F0.wireOp",EDGE,"E23.bottom");var subQ6=sQuery(id+"F0.wireOp",EDGE,"E22.right");var subQ7=sQuery(id+"F0.wireOp",EDGE,"E22.left");var subQ8=sQuery(id+"F0.wireOp",EDGE,"E22.bottom");var subQ9=sQuery(id+"F0.wireOp",EDGE,"E20");var subQ10=sQuery(id+"F0.wireOp",EDGE,"E19");var subQ11=sQuery(id+"F0.wireOp",EDGE,"E18");var subQ12=sQuery(id+"F0.wireOp",EDGE,"E16");Q0=makeQuery(id+"F10.boolean.opBoolean","MERGE",FACE,{"derivedFrom":[makeQuery(id+"F1.opExtrude","CAP_FACE",FACE,{"disambiguationData":[OSD([subQ12,subQ11,subQ10,subQ9,subQ8,subQ7,subQ6,subQ5,subQ4,subQ3,subQ2,subQ1,subQ0])],"isStart":true}),makeQuery(id+"F10.opExtrude","CAP_FACE",FACE,{"disambiguationData":[OSD([subQ12,subQ11,subQ10,subQ9,subQ8,subQ7,subQ6,subQ5,subQ4,subQ3,subQ2,subQ1,subQ0])],"isStart":false})]});}
            var sketch = newSketch(context, id + "F15", { "sketchPlane" : qUnion([Q0])});
            skLineSegment(sketch, "E98.bottom", {"start": v(-7.05, -34.5) * mm, "end": v(20.45, -34.5) * mm});
            skLineSegment(sketch, "E98.top", {"start": v(-7.05, -44.25) * mm, "end": v(20.45, -44.25) * mm});
            skLineSegment(sketch, "E98.left", {"start": v(-7.05, -34.5) * mm, "end": v(-7.05, -44.25) * mm});
            skLineSegment(sketch, "E98.right", {"start": v(20.45, -34.5) * mm, "end": v(20.45, -44.25) * mm});
            skSolve(sketch);
        }
        {
            var Q0;
            Q0 = qSketchRegion(id + "F15", true);
            extrude(context, id + "F16", {"entities" : qUnion([Q0]), "operationType" : NewBodyOperationType.REMOVE, "oppositeDirection" : true, "depth" : 0.5 * mm});
        }
        {
            var Q0;
            {var subQ0=sQuery(id+"F0.wireOp",EDGE,"E30");var subQ1=sQuery(id+"F0.wireOp",EDGE,"E29");var subQ2=sQuery(id+"F0.wireOp",EDGE,"E25.trimOffspring");var subQ3=sQuery(id+"F0.wireOp",EDGE,"E23.right");var subQ4=sQuery(id+"F0.wireOp",EDGE,"E23.left");var subQ5=sQuery(id+"F0.wireOp",EDGE,"E23.bottom");var subQ6=sQuery(id+"F0.wireOp",EDGE,"E22.right");var subQ7=sQuery(id+"F0.wireOp",EDGE,"E22.left");var subQ8=sQuery(id+"F0.wireOp",EDGE,"E22.bottom");var subQ9=sQuery(id+"F0.wireOp",EDGE,"E20");var subQ10=sQuery(id+"F0.wireOp",EDGE,"E19");var subQ11=sQuery(id+"F0.wireOp",EDGE,"E18");var subQ12=sQuery(id+"F0.wireOp",EDGE,"E16");Q0=makeQuery(id+"F10.boolean.opBoolean","MERGE",FACE,{"derivedFrom":[makeQuery(id+"F1.opExtrude","CAP_FACE",FACE,{"disambiguationData":[OSD([subQ12,subQ11,subQ10,subQ9,subQ8,subQ7,subQ6,subQ5,subQ4,subQ3,subQ2,subQ1,subQ0])],"isStart":true}),makeQuery(id+"F10.opExtrude","CAP_FACE",FACE,{"disambiguationData":[OSD([subQ12,subQ11,subQ10,subQ9,subQ8,subQ7,subQ6,subQ5,subQ4,subQ3,subQ2,subQ1,subQ0])],"isStart":false})]});}
            var sketch = newSketch(context, id + "F17", { "sketchPlane" : qUnion([Q0])});
            skLineSegment(sketch, "E99", {"start": v(-36.94, 12.5) * mm, "end": v(-34.82, 12.5) * mm});
            skLineSegment(sketch, "E100", {"start": v(-35.89, -12.5) * mm, "end": v(-35.88, -12.5) * mm});
            skLineSegment(sketch, "E101", {"start": v(0, 0) * mm, "end": v(45.74, 0) * mm, "construction": true});
            skArc(sketch, "E102.trimOffspring", {"start": v(-34.82, 12.5) * mm, "mid": v(-36.94, 2.11) * mm, "end": v(-36.02, -8.45) * mm});
            skArc(sketch, "E103.trimOffspring", {"start": v(-36.94, 12.5) * mm, "mid": v(-38.96, 1.8) * mm, "end": v(-37.94, -9.04) * mm});
            skLineSegment(sketch, "E104", {"start": v(-39.41, -9.5) * mm, "end": v(-35.88, -12.5) * mm});
            skArc(sketch, "E105.0", {"start": v(-35.77, 12.84) * mm, "mid": v(-38, 0) * mm, "end": v(-35.77, -12.84) * mm, "construction": true});
            skLineSegment(sketch, "E106", {"start": v(-35.88, -12.5) * mm, "end": v(-34.67, -8.03) * mm});
            skLineSegment(sketch, "E107", {"start": v(-34.67, -8.03) * mm, "end": v(-36.02, -8.45) * mm});
            skLineSegment(sketch, "E108.trimOffspring", {"start": v(-37.94, -9.04) * mm, "end": v(-39.41, -9.5) * mm});
            skPoint(sketch, "E109.orphan", {"position": v(-36.94, -12.5) * mm});
            skPoint(sketch, "E110.trimOffspring.end.orphan", {"position": v(-34.82, -12.5) * mm});
            skSolve(sketch);
        }
        {
            var Q0;
            Q0 = qSketchRegion(id + "F17", true);
            extrude(context, id + "F18", {"entities" : qUnion([Q0]), "operationType" : NewBodyOperationType.ADD, "depth" : 0.5 * mm});
        }
    });
